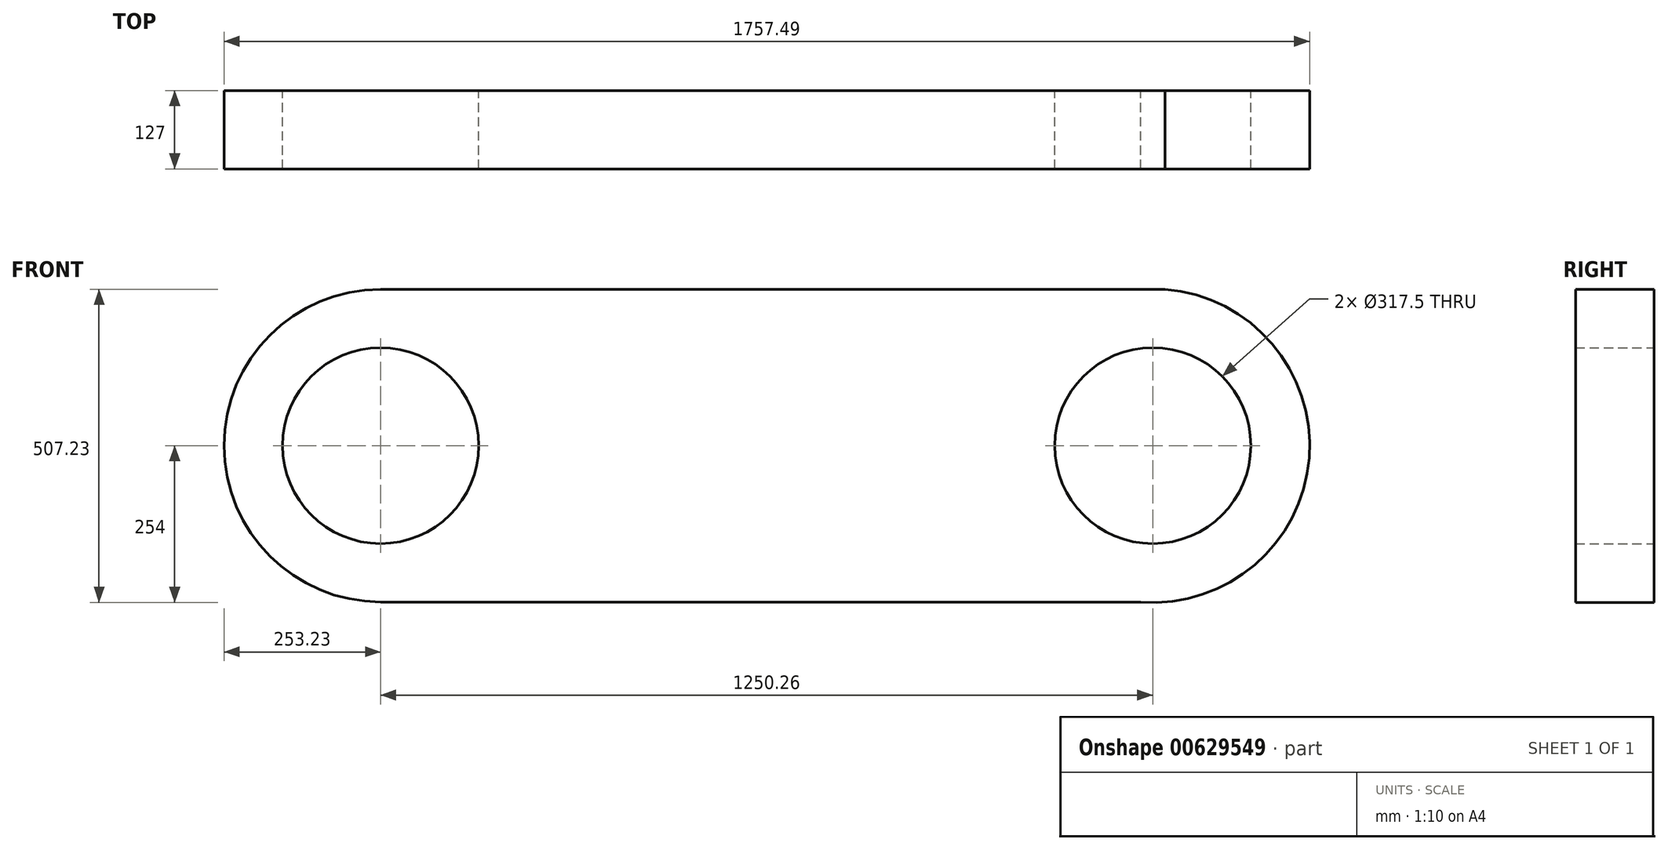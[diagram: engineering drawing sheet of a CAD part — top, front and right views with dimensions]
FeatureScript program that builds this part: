
annotation { "Feature Type Name" : "Feature", "Feature Type Description" : "" }
export const myFeature = defineFeature(function(context is Context, id is Id, definition is map)
    precondition{}
    {
        {
            var Q0;
            Q0=qCreatedBy(makeId("Front.planeOp"),FACE);
            var sketch = newSketch(context, id + "F0", { "sketchPlane" : qUnion([Q0])});
            skLineSegment(sketch, "E0.bottom", {"start": v(-615.26, 253.23) * mm, "end": v(654.74, 253.23) * mm});
            skLineSegment(sketch, "E0.top", {"start": v(-615.26, -253.23) * mm, "end": v(615.26, -253.23) * mm});
            skArc(sketch, "E1", {"start": v(-615.26, 253.23) * mm, "mid": v(-868.5, 0) * mm, "end": v(-615.26, -253.23) * mm});
            skArc(sketch, "E2", {"start": v(615.26, -253.23) * mm, "mid": v(888.23, -19.74) * mm, "end": v(654.74, 253.23) * mm});
            skCircle(sketch, "E3", {"center": v(-615.26, 0) * mm, "radius": 158.75 * mm});
            skCircle(sketch, "E4", {"center": v(635, 0) * mm, "radius": 158.75 * mm});
            skSolve(sketch);
        }
        {
            var Q0;
            Q0 = qSketchRegion(id + "F0", true);
            extrude(context, id + "F1", {"entities" : qUnion([Q0]), "depth" : 127 * mm, "offsetDistance" : 25.4 * mm});
        }
    });
